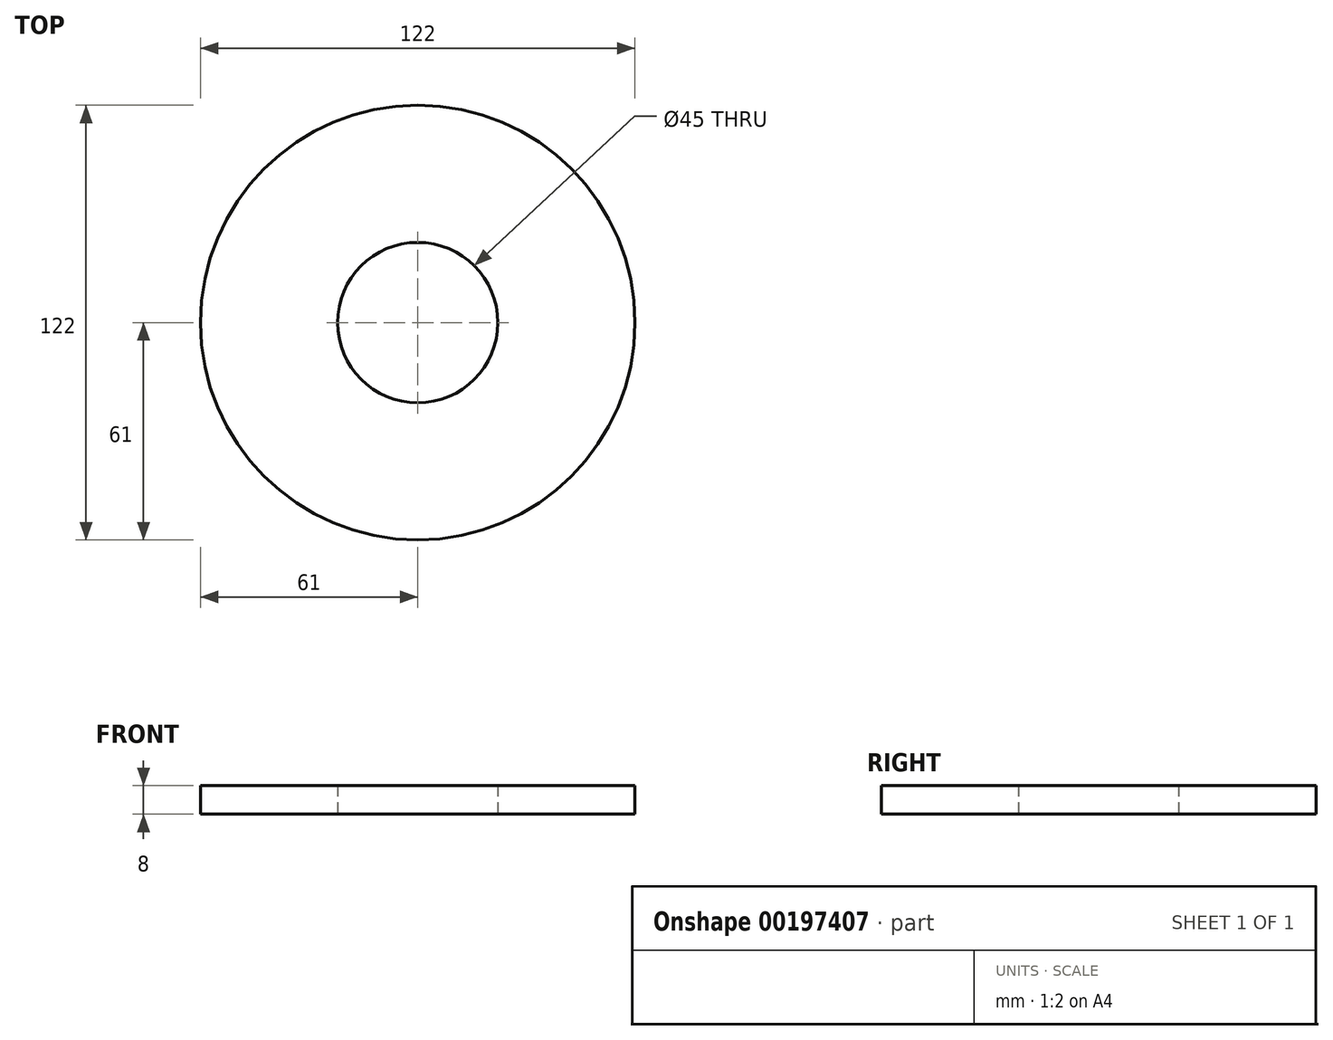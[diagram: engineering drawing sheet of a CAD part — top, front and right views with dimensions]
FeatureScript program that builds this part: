
annotation { "Feature Type Name" : "Feature", "Feature Type Description" : "" }
export const myFeature = defineFeature(function(context is Context, id is Id, definition is map)
    precondition{}
    {
        {
            var Q0;
            Q0=qCreatedBy(makeId("Top.planeOp"),FACE);
            var sketch = newSketch(context, id + "F0", { "sketchPlane" : qUnion([Q0])});
            skCircle(sketch, "E0", {"center": v(0, 0) * mm, "radius": 61 * mm});
            skCircle(sketch, "E1", {"center": v(0, 0) * mm, "radius": 22.5 * mm});
            skSolve(sketch);
        }
        {
            var Q0;
            Q0=makeQuery(id+"F0.imprint","IMPRINT",FACE,{"disambiguationData":[TD([[makeQuery(id+"F0.imprint","IMPRINT",EDGE,{"derivedFrom":sQuery(id+"F0.wireOp",EDGE,"E0")}),1.0]])]});
            extrude(context, id + "F1", {"entities" : qUnion([Q0]), "depth" : 8 * mm});
        }
    });
